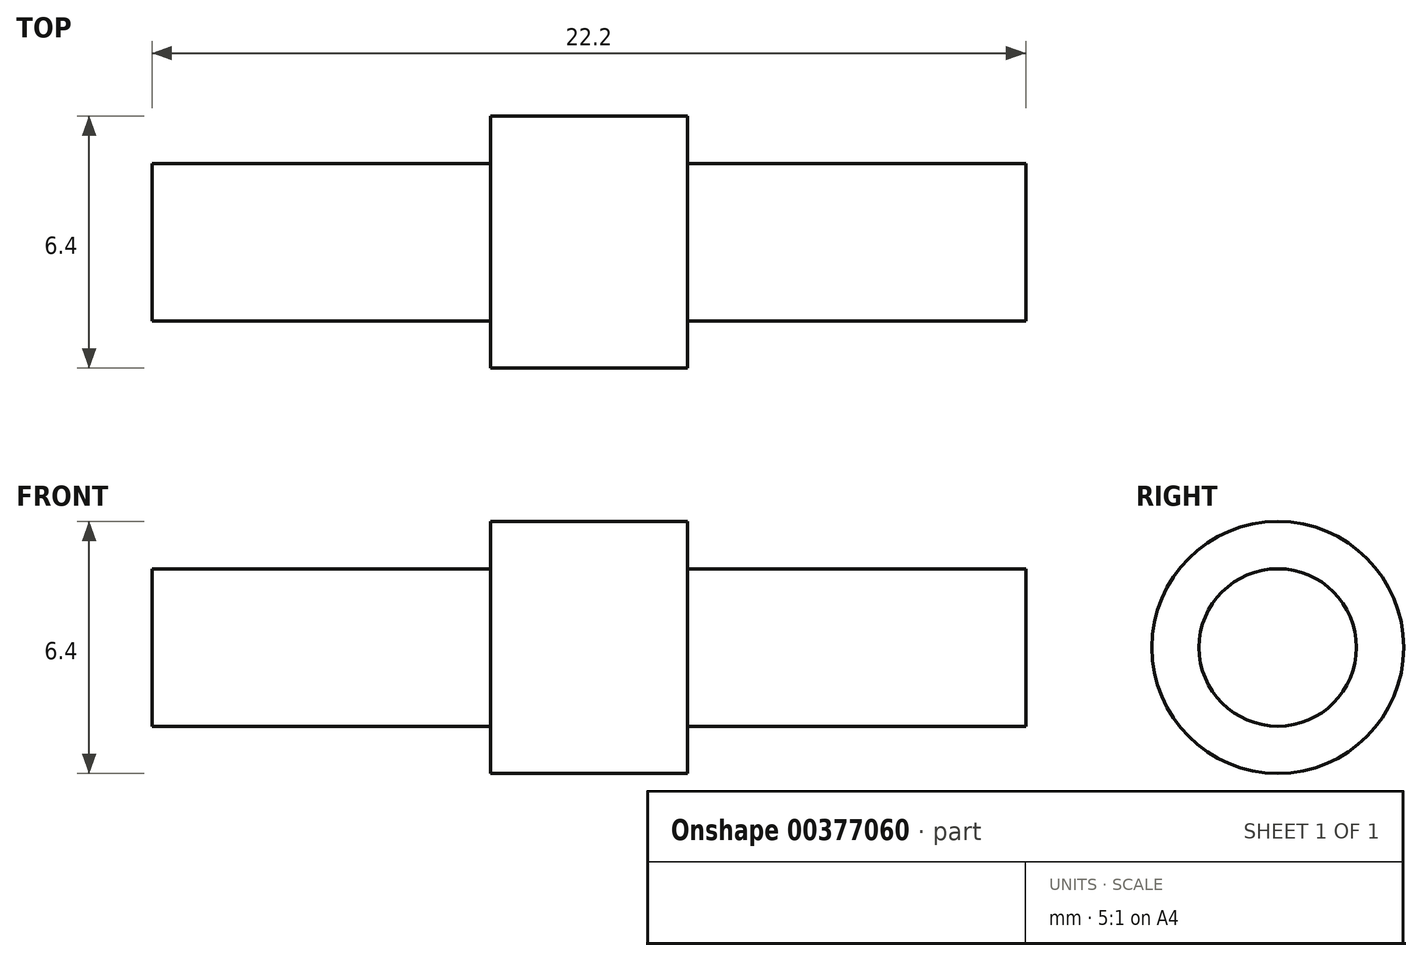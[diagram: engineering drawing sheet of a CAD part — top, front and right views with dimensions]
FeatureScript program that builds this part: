
annotation { "Feature Type Name" : "Feature", "Feature Type Description" : "" }
export const myFeature = defineFeature(function(context is Context, id is Id, definition is map)
    precondition{}
    {
        {
            var Q0;
            Q0=qCreatedBy(makeId("Front.planeOp"),FACE);
            var sketch = newSketch(context, id + "F0", { "sketchPlane" : qUnion([Q0])});
            skLineSegment(sketch, "E0", {"start": v(0, 3.6) * mm, "end": v(9.6, 3.6) * mm});
            skLineSegment(sketch, "E1", {"start": v(9.6, 2.4) * mm, "end": v(18.6, 2.4) * mm});
            skLineSegment(sketch, "E2", {"start": v(0, 2.4) * mm, "end": v(-9, 2.4) * mm});
            skCircle(sketch, "E3", {"center": v(2.7, 0) * mm, "radius": 1.5 * mm});
            skCircle(sketch, "E4", {"center": v(6.9, 0) * mm, "radius": 1.5 * mm});
            skPoint(sketch, "E5", {"position": v(1.2, 0) * mm});
            skPoint(sketch, "E6", {"position": v(4.2, 0) * mm});
            skPoint(sketch, "E7", {"position": v(5.4, 0) * mm});
            skPoint(sketch, "E8", {"position": v(8.4, 0) * mm});
            skLineSegment(sketch, "E9", {"start": v(-11.37, 1.2) * mm, "end": v(-7.92, 1.2) * mm});
            skLineSegment(sketch, "E10.bottom", {"start": v(11.2, 4.6) * mm, "end": v(13.2, 4.6) * mm});
            skLineSegment(sketch, "E10.top", {"start": v(11.2, 3.6) * mm, "end": v(13.2, 3.6) * mm});
            skLineSegment(sketch, "E10.left", {"start": v(11.2, 4.6) * mm, "end": v(11.2, 3.6) * mm});
            skLineSegment(sketch, "E10.right", {"start": v(13.2, 4.6) * mm, "end": v(13.2, 3.6) * mm});
            skLineSegment(sketch, "E11.bottom", {"start": v(-3.6, 4.6) * mm, "end": v(-1.6, 4.6) * mm});
            skLineSegment(sketch, "E11.top", {"start": v(-3.6, 3.6) * mm, "end": v(-1.6, 3.6) * mm});
            skLineSegment(sketch, "E11.left", {"start": v(-3.6, 4.6) * mm, "end": v(-3.6, 3.6) * mm});
            skLineSegment(sketch, "E11.right", {"start": v(-1.6, 4.6) * mm, "end": v(-1.6, 3.6) * mm});
            skLineSegment(sketch, "E12", {"start": v(9.6, 3.6) * mm, "end": v(11.2, 3.6) * mm, "construction": true});
            skLineSegment(sketch, "E13", {"start": v(0, 3.6) * mm, "end": v(-1.6, 3.6) * mm, "construction": true});
            skLineSegment(sketch, "E14", {"start": v(-3.6, 4.6) * mm, "end": v(-1.6, 3.6) * mm});
            skLineSegment(sketch, "E15", {"start": v(-3.6, 3.6) * mm, "end": v(-1.6, 4.6) * mm});
            skLineSegment(sketch, "E16", {"start": v(13.2, 4.6) * mm, "end": v(11.2, 3.6) * mm});
            skLineSegment(sketch, "E17", {"start": v(11.2, 4.6) * mm, "end": v(13.2, 3.6) * mm});
            skLineSegment(sketch, "E18", {"start": v(18.6, 2.2) * mm, "end": v(43, 2.2) * mm});
            skSolve(sketch);
        }
        {
            var Q0;
            Q0=qCreatedBy(makeId("Front.planeOp"),FACE);
            var sketch = newSketch(context, id + "F1", { "sketchPlane" : qUnion([Q0])});
            skLineSegment(sketch, "E19", {"start": v(4.6, 3.2) * mm, "end": v(9.6, 3.2) * mm});
            skLineSegment(sketch, "E20", {"start": v(9.6, 2) * mm, "end": v(18.2, 2) * mm});
            skLineSegment(sketch, "E21", {"start": v(9.6, 3.2) * mm, "end": v(9.6, 2) * mm});
            skLineSegment(sketch, "E22", {"start": v(18.2, 2) * mm, "end": v(18.2, 0) * mm});
            skLineSegment(sketch, "E23", {"start": v(4.6, 2) * mm, "end": v(-4, 2) * mm});
            skLineSegment(sketch, "E24", {"start": v(4.6, 3.2) * mm, "end": v(4.6, 2) * mm});
            skLineSegment(sketch, "E25", {"start": v(-4, 2) * mm, "end": v(-4, 0) * mm});
            skLineSegment(sketch, "E26", {"start": v(-4, 0) * mm, "end": v(18.2, 0) * mm});
            skSolve(sketch);
        }
        {
            var Q0;
            Q0 = qSketchRegion(id + "F1", true);
            var Q1;
            Q1=sQuery(id+"F1.wireOp",EDGE,"E26");
            revolve(context, id + "F2", {"entities" : qUnion([Q0]), "axis" : qUnion([Q1]), "revolveType" : RevolveType.FULL});
        }
    });
